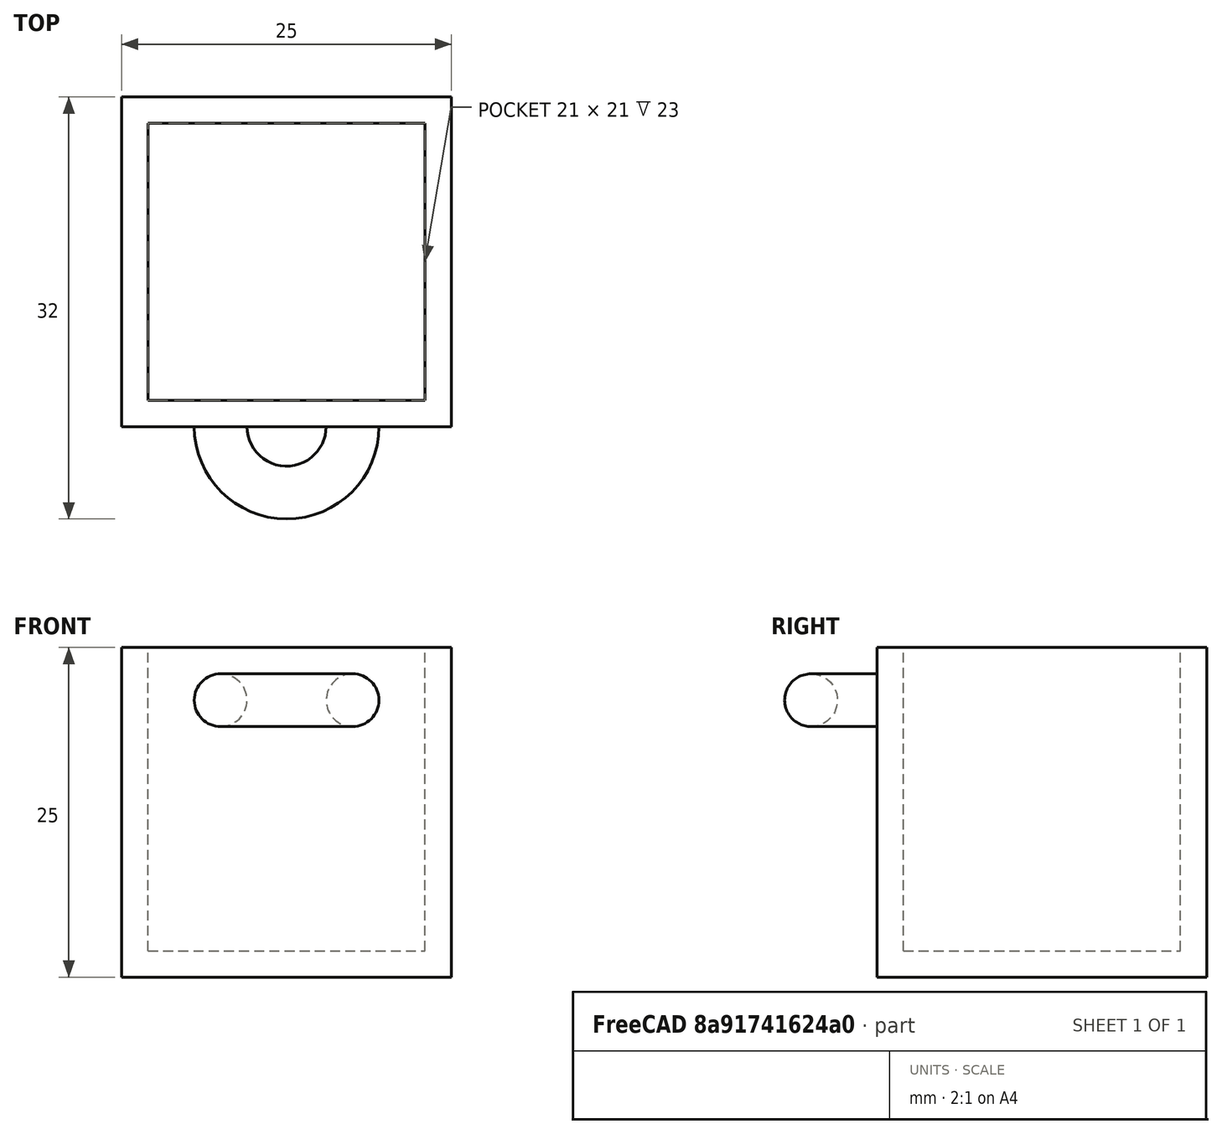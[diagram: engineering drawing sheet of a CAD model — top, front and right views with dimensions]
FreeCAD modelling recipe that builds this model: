
FCSTD DOCUMENT  (FreeCAD 0.18R16117 (Git))
Label: box ring
License: All rights reserved
LicenseURL: http://en.wikipedia.org/wiki/All_rights_reserved
objects: Part::Box×2, Part::Torus×1, Part::MultiFuse×1, Part::Cut×1
note: 5 computed .brp shape members not serialized (recipe doc carries the construction recipe); baked Part::Feature solids carry a one-line shape summary decoded from their .brp

FEATURE [Part::Box] Box  label="Cube"
  AttacherType = Attacher::AttachEngine3D
  Height = 25
  Length = 25
  Width = 25
FEATURE [Part::Box] Box001  label="Cube001"
  AttacherType = Attacher::AttachEngine3D
  Height = 24
  Length = 21
  Placement = pos=(2,2,2) rot=(0,0,1;0rad)
  Width = 21
FEATURE [Part::Torus] Torus
  Angle1 = -180
  Angle2 = 180
  Angle3 = 360
  AttacherType = Attacher::AttachEngine3D
  Placement = pos=(12.5,0,21) rot=(0,0,1;0rad)
  Radius1 = 5
  Radius2 = 2
FEATURE [Part::MultiFuse] Fusion
  Shapes = -> [Box,Torus]
FEATURE [Part::Cut] Cut
  Base = -> Fusion
  Tool = -> Box001
